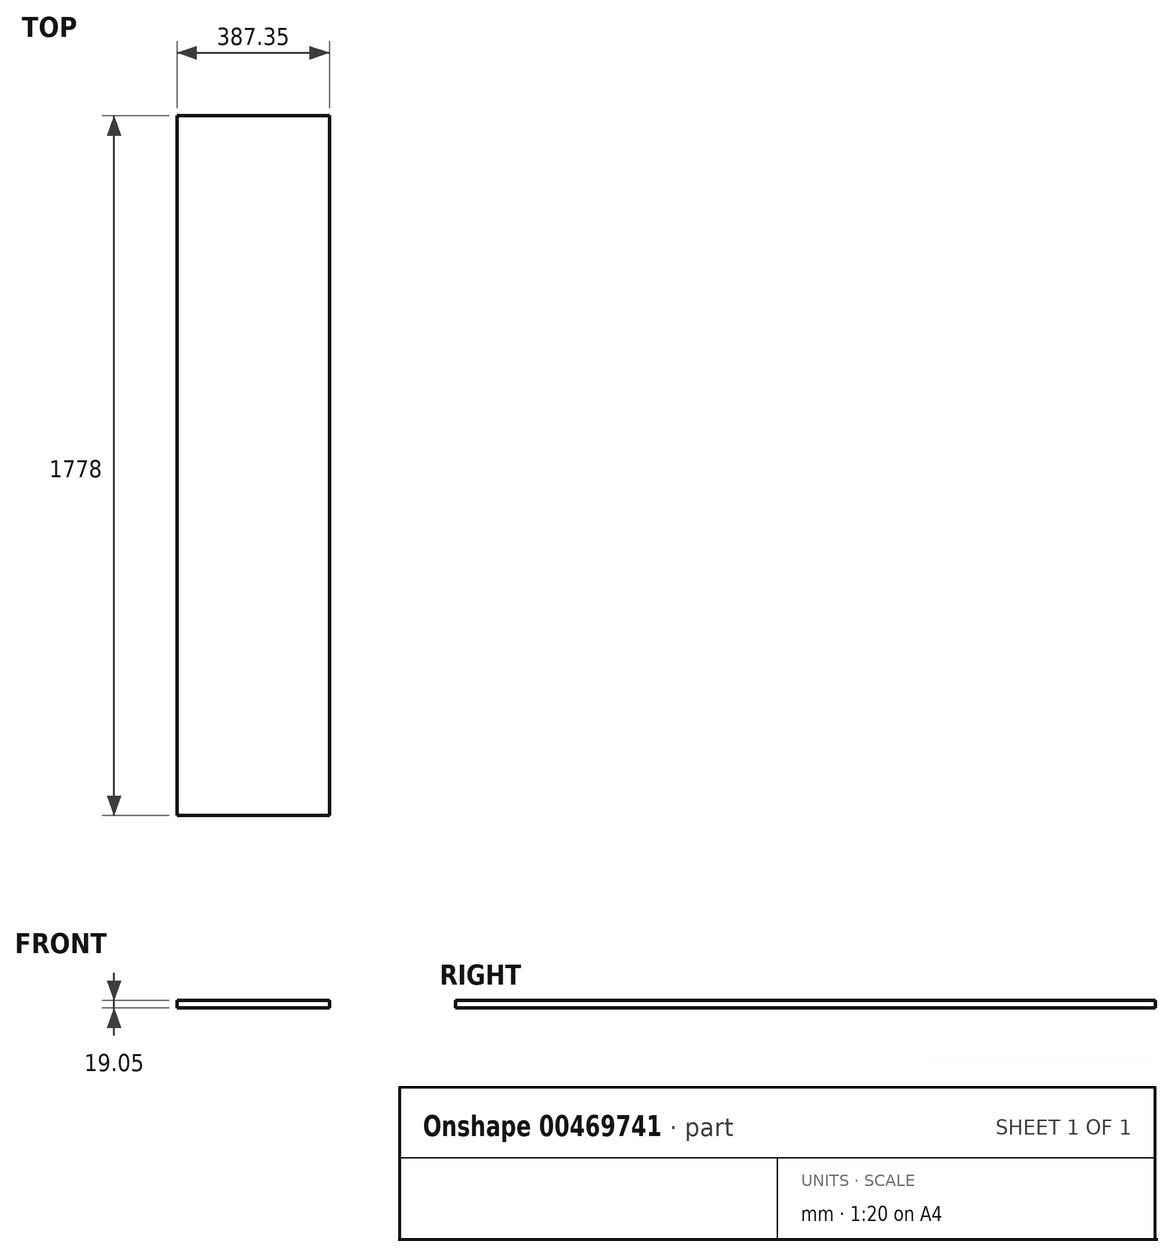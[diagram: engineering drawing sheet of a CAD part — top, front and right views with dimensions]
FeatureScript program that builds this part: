
annotation { "Feature Type Name" : "Feature", "Feature Type Description" : "" }
export const myFeature = defineFeature(function(context is Context, id is Id, definition is map)
    precondition{}
    {
        {
            var Q0;
            Q0=qCreatedBy(makeId("Right.planeOp"),FACE);
            var sketch = newSketch(context, id + "F0", { "sketchPlane" : qUnion([Q0])});
            skLineSegment(sketch, "E0.bottom", {"start": v(0, 0) * mm, "end": v(1778, 0) * mm});
            skLineSegment(sketch, "E0.top", {"start": v(0, 19.05) * mm, "end": v(1778, 19.05) * mm});
            skLineSegment(sketch, "E0.left", {"start": v(0, 0) * mm, "end": v(0, 19.05) * mm});
            skLineSegment(sketch, "E0.right", {"start": v(1778, 0) * mm, "end": v(1778, 19.05) * mm});
            skSolve(sketch);
        }
        {
            var Q0;
            Q0=makeQuery(id+"F0.imprint","IMPRINT",FACE,{"disambiguationData":[TD([[makeQuery(id+"F0.imprint","IMPRINT",EDGE,{"derivedFrom":sQuery(id+"F0.wireOp",EDGE,"E0.bottom")}),1.0]])]});
            extrude(context, id + "F1", {"entities" : qUnion([Q0]), "depth" : 387.35 * mm, "offsetDistance" : 25.4 * mm});
        }
    });
